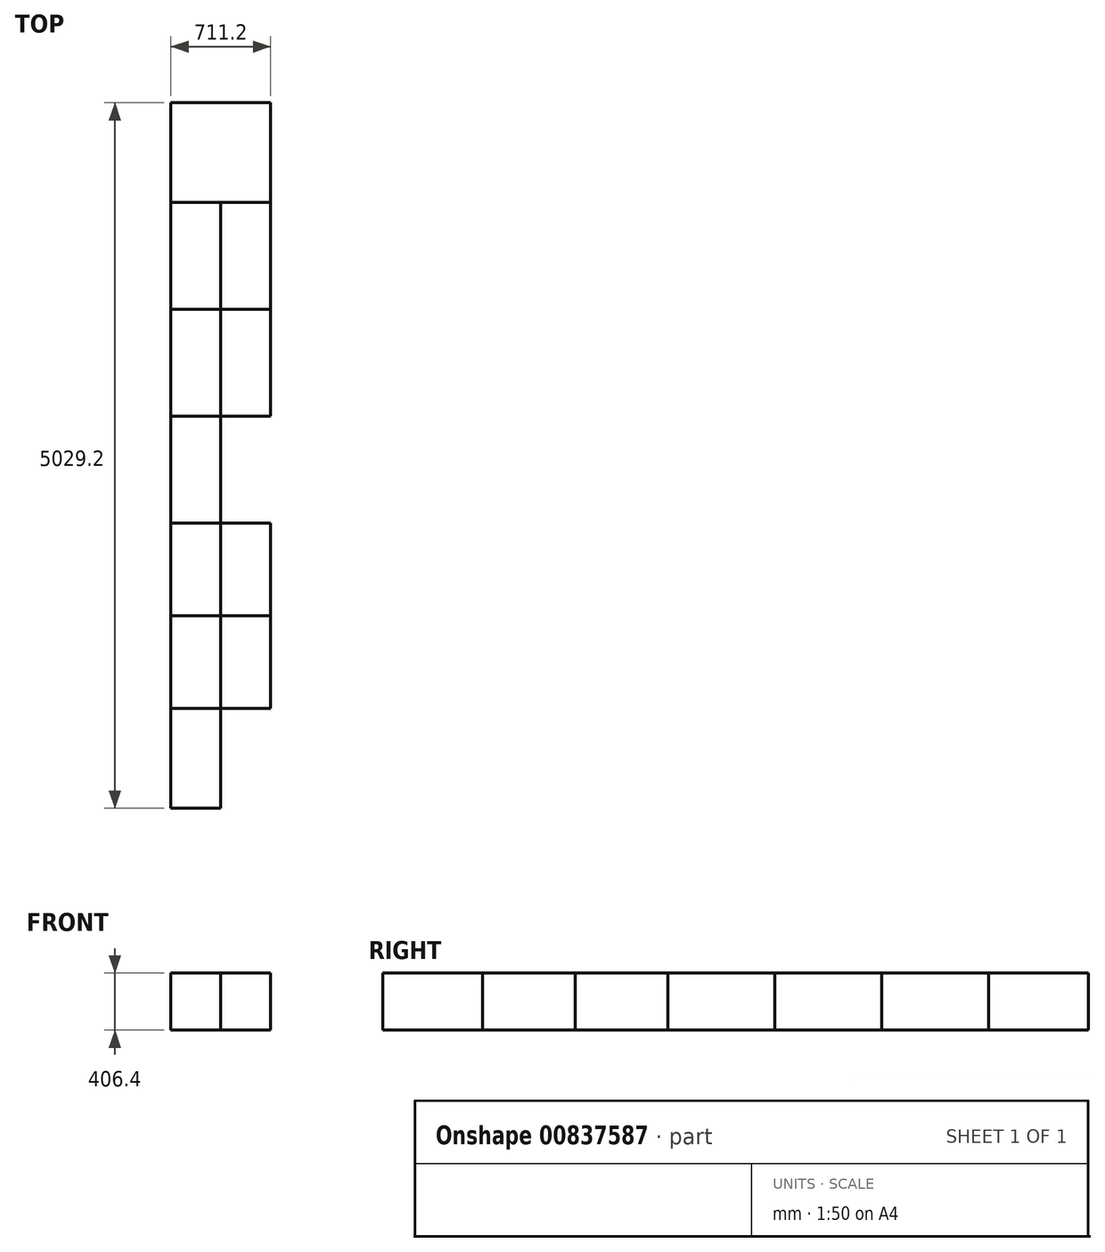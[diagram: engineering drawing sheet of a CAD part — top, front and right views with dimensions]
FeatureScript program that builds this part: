
annotation { "Feature Type Name" : "Feature", "Feature Type Description" : "" }
export const myFeature = defineFeature(function(context is Context, id is Id, definition is map)
    precondition{}
    {
        {
            var Q0;
            Q0=qCreatedBy(makeId("Top.planeOp"),FACE);
            var sketch = newSketch(context, id + "F0", { "sketchPlane" : qUnion([Q0])});
            skLineSegment(sketch, "E0.bottom", {"start": v(-355.6, 2159) * mm, "end": v(355.6, 2159) * mm});
            skLineSegment(sketch, "E0.top", {"start": v(-355.6, -2159) * mm, "end": v(355.6, -2159) * mm});
            skLineSegment(sketch, "E0.left", {"start": v(-355.6, 2159) * mm, "end": v(-355.6, -2159) * mm});
            skLineSegment(sketch, "E0.right", {"start": v(355.6, 2159) * mm, "end": v(355.6, -2159) * mm});
            skPoint(sketch, "E0.middle", {"position": v(0, 0) * mm});
            skLineSegment(sketch, "E1.top", {"start": v(-355.6, -1447.8) * mm, "end": v(355.6, -1447.8) * mm});
            skLineSegment(sketch, "E1.left", {"start": v(-355.6, -2159) * mm, "end": v(-355.6, -1447.8) * mm});
            skLineSegment(sketch, "E1.right", {"start": v(355.6, -2159) * mm, "end": v(355.6, -1447.8) * mm});
            skLineSegment(sketch, "E2.top", {"start": v(-355.6, -787.4) * mm, "end": v(355.6, -787.4) * mm});
            skLineSegment(sketch, "E2.left", {"start": v(-355.6, -1447.8) * mm, "end": v(-355.6, -787.4) * mm});
            skLineSegment(sketch, "E2.right", {"start": v(355.6, -1447.8) * mm, "end": v(355.6, -787.4) * mm});
            skLineSegment(sketch, "E3.bottom", {"start": v(-355.6, -127) * mm, "end": v(355.6, -127) * mm});
            skLineSegment(sketch, "E3.left", {"start": v(-355.6, -127) * mm, "end": v(-355.6, -787.4) * mm});
            skLineSegment(sketch, "E3.right", {"start": v(355.6, -127) * mm, "end": v(355.6, -787.4) * mm});
            skLineSegment(sketch, "E4.top", {"start": v(-355.6, 635) * mm, "end": v(355.6, 635) * mm});
            skLineSegment(sketch, "E4.left", {"start": v(-355.6, 635) * mm, "end": v(-355.6, 0) * mm});
            skLineSegment(sketch, "E4.right", {"start": v(355.6, 635) * mm, "end": v(355.6, 0) * mm});
            skLineSegment(sketch, "E5.bottom", {"start": v(-355.6, 1397) * mm, "end": v(355.6, 1397) * mm});
            skLineSegment(sketch, "E5.left", {"start": v(-355.6, 1397) * mm, "end": v(-355.6, 0) * mm});
            skLineSegment(sketch, "E5.right", {"start": v(355.6, 1397) * mm, "end": v(355.6, 0) * mm});
            skLineSegment(sketch, "E6.left", {"start": v(-355.6, 2159) * mm, "end": v(-355.6, 1397) * mm});
            skLineSegment(sketch, "E6.right", {"start": v(355.6, 2159) * mm, "end": v(355.6, 1397) * mm});
            skLineSegment(sketch, "E7.top", {"start": v(-355.6, 2870.2) * mm, "end": v(355.6, 2870.2) * mm});
            skLineSegment(sketch, "E7.left", {"start": v(-355.6, 2159) * mm, "end": v(-355.6, 2870.2) * mm});
            skLineSegment(sketch, "E7.right", {"start": v(355.6, 2159) * mm, "end": v(355.6, 2870.2) * mm});
            skLineSegment(sketch, "E8", {"start": v(0, -2159) * mm, "end": v(0, 2870.2) * mm});
            skSolve(sketch);
        }
        {
            var Q0;
            Q0=makeQuery(id+"F0.imprint","IMPRINT",FACE,{"disambiguationData":[TD([[makeQuery(id+"F0.imprint","IMPRINT",EDGE,{"derivedFrom":sQuery(id+"F0.wireOp",EDGE,"E1.top")}),1.0]])]});
            extrude(context, id + "F1", {"entities" : qUnion([Q0]), "depth" : 406.4 * mm, "offsetDistance" : 25.4 * mm});
        }
        {
            var Q0;
            Q0=makeQuery(id+"F0.imprint","IMPRINT",FACE,{"disambiguationData":[TD([[makeQuery(id+"F0.imprint","IMPRINT",EDGE,{"derivedFrom":sQuery(id+"F0.wireOp",EDGE,"E3.bottom")}),-1.0]])]});
            extrude(context, id + "F2", {"entities" : qUnion([Q0]), "depth" : 406.4 * mm, "offsetDistance" : 25.4 * mm});
        }
        {
            var Q0;
            {var subQ2=sQuery(id+"F0.wireOp",EDGE,"E0.left");Q0=makeQuery(id+"F0.imprint","IMPRINT",FACE,{"disambiguationData":[TD([[makeQuery(id+"F0.imprint","IMPRINT",EDGE,{"derivedFrom":subQ2}),1.0]])]});}
            extrude(context, id + "F3", {"entities" : qUnion([Q0]), "depth" : 406.4 * mm, "offsetDistance" : 25.4 * mm});
        }
        {
            var Q0;
            {var subQ0=sQuery(id+"F0.wireOp",EDGE,"E4.top");Q0=makeQuery(id+"F0.imprint","IMPRINT",FACE,{"disambiguationData":[TD([[makeQuery(id+"F0.imprint","IMPRINT",EDGE,{"derivedFrom":subQ0}),1.0]])]});}
            extrude(context, id + "F4", {"entities" : qUnion([Q0]), "depth" : 406.4 * mm, "offsetDistance" : 25.4 * mm});
        }
        {
            var Q0;
            Q0=makeQuery(id+"F0.imprint","IMPRINT",FACE,{"disambiguationData":[TD([[makeQuery(id+"F0.imprint","IMPRINT",EDGE,{"derivedFrom":sQuery(id+"F0.wireOp",EDGE,"E5.bottom")}),1.0]])]});
            extrude(context, id + "F5", {"entities" : qUnion([Q0]), "depth" : 406.4 * mm, "offsetDistance" : 25.4 * mm});
        }
        {
            var Q0;
            Q0=makeQuery(id+"F0.imprint","IMPRINT",FACE,{"disambiguationData":[TD([[makeQuery(id+"F0.imprint","IMPRINT",EDGE,{"derivedFrom":sQuery(id+"F0.wireOp",EDGE,"E0.bottom")}),1.0]])]});
            extrude(context, id + "F6", {"entities" : qUnion([Q0]), "depth" : 406.4 * mm, "offsetDistance" : 25.4 * mm});
        }
        {
            var Q0;
            {var subQ0=sQuery(id+"F0.wireOp",EDGE,"E1.right");Q0=makeQuery(id+"F0.imprint","IMPRINT",FACE,{"disambiguationData":[TD([[makeQuery(id+"F0.imprint","IMPRINT",EDGE,{"derivedFrom":subQ0}),1.0]])]});}
            var Q1;
            Q1=sQuery(id+"F0.wireOp",EDGE,"E8");
            extrude(context, id + "F7", {"entities" : qUnion([Q0]), "bodyType" : ToolBodyType.SURFACE, "surfaceEntities" : qUnion([Q1]), "depth" : 508 * mm, "offsetDistance" : 25.4 * mm});
        }
    });
